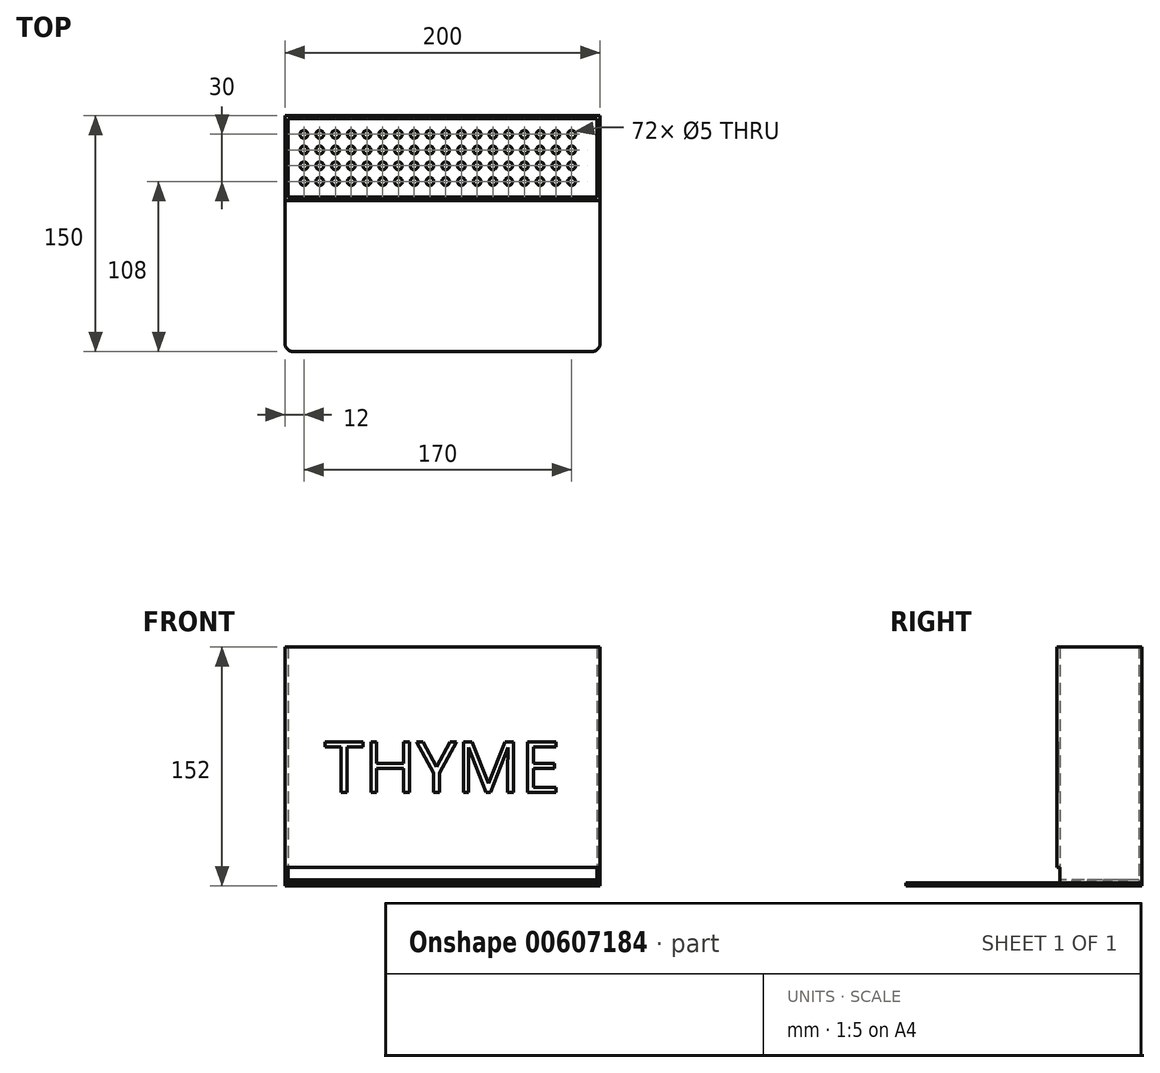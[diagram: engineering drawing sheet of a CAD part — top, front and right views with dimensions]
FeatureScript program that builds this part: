
annotation { "Feature Type Name" : "Feature", "Feature Type Description" : "" }
export const myFeature = defineFeature(function(context is Context, id is Id, definition is map)
    precondition{}
    {
        {
            var Q0;
            Q0=qCreatedBy(makeId("Top.planeOp"),FACE);
            var sketch = newSketch(context, id + "F0", { "sketchPlane" : qUnion([Q0])});
            skLineSegment(sketch, "E0.bottom", {"start": v(0, 0) * mm, "end": v(200, 0) * mm});
            skLineSegment(sketch, "E0.top", {"start": v(0, -150) * mm, "end": v(200, -150) * mm});
            skLineSegment(sketch, "E0.left", {"start": v(0, 0) * mm, "end": v(0, -150) * mm});
            skLineSegment(sketch, "E0.right", {"start": v(200, 0) * mm, "end": v(200, -150) * mm});
            skSolve(sketch);
        }
        {
            var Q0;
            Q0=makeQuery(id+"F0.imprint","IMPRINT",FACE,{"disambiguationData":[TD([[makeQuery(id+"F0.imprint","IMPRINT",EDGE,{"derivedFrom":sQuery(id+"F0.wireOp",EDGE,"E0.bottom")}),-1.0]])]});
            extrude(context, id + "F1", {"entities" : qUnion([Q0]), "depth" : 2 * mm, "offsetDistance" : 25 * mm});
        }
        {
            var Q0;
            Q0=makeQuery(id+"F1.opExtrude","CAP_FACE",FACE,{"disambiguationData":[OSD([sQuery(id+"F0.wireOp",EDGE,"E0.bottom"),sQuery(id+"F0.wireOp",EDGE,"E0.top"),sQuery(id+"F0.wireOp",EDGE,"E0.left"),sQuery(id+"F0.wireOp",EDGE,"E0.right")])],"isStart":false});
            var sketch = newSketch(context, id + "F2", { "sketchPlane" : qUnion([Q0])});
            skLineSegment(sketch, "E1.bottom", {"start": v(0, 0) * mm, "end": v(200, 0) * mm});
            skLineSegment(sketch, "E1.top", {"start": v(0, -2) * mm, "end": v(200, -2) * mm});
            skLineSegment(sketch, "E1.left", {"start": v(0, 0) * mm, "end": v(0, -2) * mm});
            skLineSegment(sketch, "E1.right", {"start": v(200, 0) * mm, "end": v(200, -2) * mm});
            skLineSegment(sketch, "E2.bottom", {"start": v(0, -2) * mm, "end": v(2, -2) * mm});
            skLineSegment(sketch, "E2.top", {"start": v(0, -52) * mm, "end": v(2, -52) * mm});
            skLineSegment(sketch, "E2.left", {"start": v(0, -2) * mm, "end": v(0, -52) * mm});
            skLineSegment(sketch, "E2.right", {"start": v(2, -2) * mm, "end": v(2, -52) * mm});
            skLineSegment(sketch, "E3.bottom", {"start": v(200, -2) * mm, "end": v(198, -2) * mm});
            skLineSegment(sketch, "E3.top", {"start": v(200, -52) * mm, "end": v(198, -52) * mm});
            skLineSegment(sketch, "E3.left", {"start": v(200, -2) * mm, "end": v(200, -52) * mm});
            skLineSegment(sketch, "E3.right", {"start": v(198, -2) * mm, "end": v(198, -52) * mm});
            skLineSegment(sketch, "E4.bottom", {"start": v(0, -52) * mm, "end": v(200, -52) * mm});
            skLineSegment(sketch, "E4.top", {"start": v(0, -54) * mm, "end": v(200, -54) * mm});
            skLineSegment(sketch, "E4.left", {"start": v(0, -52) * mm, "end": v(0, -54) * mm});
            skLineSegment(sketch, "E4.right", {"start": v(200, -52) * mm, "end": v(200, -54) * mm});
            skSolve(sketch);
        }
        {
            var Q0;
            Q0 = qSketchRegion(id + "F2", true);
            extrude(context, id + "F3", {"entities" : qUnion([Q0]), "depth" : 150 * mm, "offsetDistance" : 25 * mm});
        }
        {
            var Q0;
            Q0=makeQuery(id+"F3.opExtrude","SWEPT_FACE",FACE,{"disambiguationData":[OSD([sQuery(id+"F2.wireOp",EDGE,"E4.top")])]});
            var sketch = newSketch(context, id + "F4", { "sketchPlane" : qUnion([Q0])});
            skText(sketch, "E5", { "text": "THYME", "fontName": "OpenSans-Regular.ttf"});
            const initialGuessF4  = {"E5": [0.025, 0.05942, 1, 0, 0.03258]};
            skSetInitialGuess(sketch, initialGuessF4);
            skSolve(sketch);
        }
        {
            var Q0;
            Q0=makeQuery(id+"F3.boolean.opBoolean","SPLIT",FACE,{"disambiguationData":[TD([makeQuery(id+"F3.opExtrude","SWEPT_FACE",FACE,{"disambiguationData":[OSD([sQuery(id+"F2.wireOp",EDGE,"E1.top")])]})])],"derivedFrom":makeQuery(id+"F1.opExtrude","CAP_FACE",FACE,{"disambiguationData":[OSD([sQuery(id+"F0.wireOp",EDGE,"E0.bottom"),sQuery(id+"F0.wireOp",EDGE,"E0.top"),sQuery(id+"F0.wireOp",EDGE,"E0.left"),sQuery(id+"F0.wireOp",EDGE,"E0.right")])],"isStart":false})});
            var sketch = newSketch(context, id + "F5", { "sketchPlane" : qUnion([Q0])});
            skLineSegment(sketch, "E6.bottom", {"start": v(2, -2) * mm, "end": v(198, -2) * mm});
            skLineSegment(sketch, "E6.top", {"start": v(2, -52) * mm, "end": v(198, -52) * mm});
            skLineSegment(sketch, "E6.left", {"start": v(2, -2) * mm, "end": v(2, -52) * mm});
            skLineSegment(sketch, "E6.right", {"start": v(198, -2) * mm, "end": v(198, -52) * mm});
            skCircle(sketch, "E7", {"center": v(12, -12) * mm, "radius": 2.5 * mm});
            skCircle(sketch, "E8.0.1.0", {"center": v(12, -22) * mm, "radius": 2.5 * mm});
            skCircle(sketch, "E8.0.2.0", {"center": v(12, -32) * mm, "radius": 2.5 * mm});
            skCircle(sketch, "E8.0.3.0", {"center": v(12, -42) * mm, "radius": 2.5 * mm});
            skCircle(sketch, "E8.1.0.0", {"center": v(22, -12) * mm, "radius": 2.5 * mm});
            skCircle(sketch, "E8.1.1.0", {"center": v(22, -22) * mm, "radius": 2.5 * mm});
            skCircle(sketch, "E8.1.2.0", {"center": v(22, -32) * mm, "radius": 2.5 * mm});
            skCircle(sketch, "E8.1.3.0", {"center": v(22, -42) * mm, "radius": 2.5 * mm});
            skCircle(sketch, "E8.2.0.0", {"center": v(32, -12) * mm, "radius": 2.5 * mm});
            skCircle(sketch, "E8.2.1.0", {"center": v(32, -22) * mm, "radius": 2.5 * mm});
            skCircle(sketch, "E8.2.2.0", {"center": v(32, -32) * mm, "radius": 2.5 * mm});
            skCircle(sketch, "E8.2.3.0", {"center": v(32, -42) * mm, "radius": 2.5 * mm});
            skCircle(sketch, "E8.3.0.0", {"center": v(42, -12) * mm, "radius": 2.5 * mm});
            skCircle(sketch, "E8.3.1.0", {"center": v(42, -22) * mm, "radius": 2.5 * mm});
            skCircle(sketch, "E8.3.2.0", {"center": v(42, -32) * mm, "radius": 2.5 * mm});
            skCircle(sketch, "E8.3.3.0", {"center": v(42, -42) * mm, "radius": 2.5 * mm});
            skCircle(sketch, "E8.4.0.0", {"center": v(52, -12) * mm, "radius": 2.5 * mm});
            skCircle(sketch, "E8.4.1.0", {"center": v(52, -22) * mm, "radius": 2.5 * mm});
            skCircle(sketch, "E8.4.2.0", {"center": v(52, -32) * mm, "radius": 2.5 * mm});
            skCircle(sketch, "E8.4.3.0", {"center": v(52, -42) * mm, "radius": 2.5 * mm});
            skCircle(sketch, "E8.5.0.0", {"center": v(62, -12) * mm, "radius": 2.5 * mm});
            skCircle(sketch, "E8.5.1.0", {"center": v(62, -22) * mm, "radius": 2.5 * mm});
            skCircle(sketch, "E8.5.2.0", {"center": v(62, -32) * mm, "radius": 2.5 * mm});
            skCircle(sketch, "E8.5.3.0", {"center": v(62, -42) * mm, "radius": 2.5 * mm});
            skCircle(sketch, "E8.6.0.0", {"center": v(72, -12) * mm, "radius": 2.5 * mm});
            skCircle(sketch, "E8.6.1.0", {"center": v(72, -22) * mm, "radius": 2.5 * mm});
            skCircle(sketch, "E8.6.2.0", {"center": v(72, -32) * mm, "radius": 2.5 * mm});
            skCircle(sketch, "E8.6.3.0", {"center": v(72, -42) * mm, "radius": 2.5 * mm});
            skCircle(sketch, "E8.7.0.0", {"center": v(82, -12) * mm, "radius": 2.5 * mm});
            skCircle(sketch, "E8.7.1.0", {"center": v(82, -22) * mm, "radius": 2.5 * mm});
            skCircle(sketch, "E8.7.2.0", {"center": v(82, -32) * mm, "radius": 2.5 * mm});
            skCircle(sketch, "E8.7.3.0", {"center": v(82, -42) * mm, "radius": 2.5 * mm});
            skCircle(sketch, "E8.8.0.0", {"center": v(92, -12) * mm, "radius": 2.5 * mm});
            skCircle(sketch, "E8.8.1.0", {"center": v(92, -22) * mm, "radius": 2.5 * mm});
            skCircle(sketch, "E8.8.2.0", {"center": v(92, -32) * mm, "radius": 2.5 * mm});
            skCircle(sketch, "E8.8.3.0", {"center": v(92, -42) * mm, "radius": 2.5 * mm});
            skCircle(sketch, "E8.9.0.0", {"center": v(102, -12) * mm, "radius": 2.5 * mm});
            skCircle(sketch, "E8.9.1.0", {"center": v(102, -22) * mm, "radius": 2.5 * mm});
            skCircle(sketch, "E8.9.2.0", {"center": v(102, -32) * mm, "radius": 2.5 * mm});
            skCircle(sketch, "E8.9.3.0", {"center": v(102, -42) * mm, "radius": 2.5 * mm});
            skCircle(sketch, "E8.10.0.0", {"center": v(112, -12) * mm, "radius": 2.5 * mm});
            skCircle(sketch, "E8.10.1.0", {"center": v(112, -22) * mm, "radius": 2.5 * mm});
            skCircle(sketch, "E8.10.2.0", {"center": v(112, -32) * mm, "radius": 2.5 * mm});
            skCircle(sketch, "E8.10.3.0", {"center": v(112, -42) * mm, "radius": 2.5 * mm});
            skCircle(sketch, "E8.11.0.0", {"center": v(122, -12) * mm, "radius": 2.5 * mm});
            skCircle(sketch, "E8.11.1.0", {"center": v(122, -22) * mm, "radius": 2.5 * mm});
            skCircle(sketch, "E8.11.2.0", {"center": v(122, -32) * mm, "radius": 2.5 * mm});
            skCircle(sketch, "E8.11.3.0", {"center": v(122, -42) * mm, "radius": 2.5 * mm});
            skCircle(sketch, "E8.12.0.0", {"center": v(132, -12) * mm, "radius": 2.5 * mm});
            skCircle(sketch, "E8.12.1.0", {"center": v(132, -22) * mm, "radius": 2.5 * mm});
            skCircle(sketch, "E8.12.2.0", {"center": v(132, -32) * mm, "radius": 2.5 * mm});
            skCircle(sketch, "E8.12.3.0", {"center": v(132, -42) * mm, "radius": 2.5 * mm});
            skCircle(sketch, "E8.13.0.0", {"center": v(142, -12) * mm, "radius": 2.5 * mm});
            skCircle(sketch, "E8.13.1.0", {"center": v(142, -22) * mm, "radius": 2.5 * mm});
            skCircle(sketch, "E8.13.2.0", {"center": v(142, -32) * mm, "radius": 2.5 * mm});
            skCircle(sketch, "E8.13.3.0", {"center": v(142, -42) * mm, "radius": 2.5 * mm});
            skCircle(sketch, "E8.14.0.0", {"center": v(152, -12) * mm, "radius": 2.5 * mm});
            skCircle(sketch, "E8.14.1.0", {"center": v(152, -22) * mm, "radius": 2.5 * mm});
            skCircle(sketch, "E8.14.2.0", {"center": v(152, -32) * mm, "radius": 2.5 * mm});
            skCircle(sketch, "E8.14.3.0", {"center": v(152, -42) * mm, "radius": 2.5 * mm});
            skCircle(sketch, "E8.15.0.0", {"center": v(162, -12) * mm, "radius": 2.5 * mm});
            skCircle(sketch, "E8.15.1.0", {"center": v(162, -22) * mm, "radius": 2.5 * mm});
            skCircle(sketch, "E8.15.2.0", {"center": v(162, -32) * mm, "radius": 2.5 * mm});
            skCircle(sketch, "E8.15.3.0", {"center": v(162, -42) * mm, "radius": 2.5 * mm});
            skCircle(sketch, "E8.16.0.0", {"center": v(172, -12) * mm, "radius": 2.5 * mm});
            skCircle(sketch, "E8.16.1.0", {"center": v(172, -22) * mm, "radius": 2.5 * mm});
            skCircle(sketch, "E8.16.2.0", {"center": v(172, -32) * mm, "radius": 2.5 * mm});
            skCircle(sketch, "E8.16.3.0", {"center": v(172, -42) * mm, "radius": 2.5 * mm});
            skCircle(sketch, "E8.17.0.0", {"center": v(182, -12) * mm, "radius": 2.5 * mm});
            skCircle(sketch, "E8.17.1.0", {"center": v(182, -22) * mm, "radius": 2.5 * mm});
            skCircle(sketch, "E8.17.2.0", {"center": v(182, -32) * mm, "radius": 2.5 * mm});
            skCircle(sketch, "E8.17.3.0", {"center": v(182, -42) * mm, "radius": 2.5 * mm});
            skLineSegment(sketch, "E8.direction1", {"start": v(12, -12) * mm, "end": v(22, -12) * mm, "construction": true});
            skLineSegment(sketch, "E8.direction2", {"start": v(12, -12) * mm, "end": v(12, -22) * mm, "construction": true});
            skSolve(sketch);
        }
        {
            var Q0;
            Q0 = qSketchRegion(id + "F5", true);
            extrude(context, id + "F6", {"entities" : qUnion([Q0]), "depth" : 2 * mm, "offsetDistance" : 25 * mm});
        }
        {
            var Q0;
            Q0 = qSketchRegion(id + "F4", true);
            extrude(context, id + "F7", {"entities" : qUnion([Q0]), "operationType" : NewBodyOperationType.REMOVE, "oppositeDirection" : true, "depth" : 1 * mm, "offsetDistance" : 25 * mm});
        }
        {
            var Q0;
            Q0=makeQuery(id+"F1.opExtrude","SWEPT_EDGE",EDGE,{"disambiguationData":[OSD([sQuery(id+"F0.wireOp",EDGE,"E0.top"),sQuery(id+"F0.wireOp",EDGE,"E0.right")])]});
            fillet(context, id + "F8", {"entities" : qUnion([Q0]), "radius" : 5 * mm, "tangentPropagation" : true, "allowEdgeOverflow" : false});
        }
        {
            var Q0;
            Q0=makeQuery(id+"F1.opExtrude","SWEPT_EDGE",EDGE,{"disambiguationData":[OSD([sQuery(id+"F0.wireOp",EDGE,"E0.top"),sQuery(id+"F0.wireOp",EDGE,"E0.left")])]});
            fillet(context, id + "F9", {"entities" : qUnion([Q0]), "radius" : 5 * mm, "tangentPropagation" : true, "allowEdgeOverflow" : false});
        }
        {
            var Q0;
            Q0=makeQuery(id+"F3.opExtrude","SWEPT_FACE",FACE,{"disambiguationData":[OSD([sQuery(id+"F2.wireOp",EDGE,"E4.top")])]});
            var sketch = newSketch(context, id + "F10", { "sketchPlane" : qUnion([Q0])});
            skLineSegment(sketch, "E9.bottom", {"start": v(0, 2) * mm, "end": v(200, 2) * mm});
            skLineSegment(sketch, "E9.top", {"start": v(0, 12) * mm, "end": v(200, 12) * mm});
            skLineSegment(sketch, "E9.left", {"start": v(0, 2) * mm, "end": v(0, 12) * mm});
            skLineSegment(sketch, "E9.right", {"start": v(200, 2) * mm, "end": v(200, 12) * mm});
            skSolve(sketch);
        }
        {
            var Q0;
            Q0 = qSketchRegion(id + "F10", true);
            extrude(context, id + "F11", {"entities" : qUnion([Q0]), "operationType" : NewBodyOperationType.REMOVE, "oppositeDirection" : true, "depth" : 2 * mm, "offsetDistance" : 25 * mm});
        }
    });
